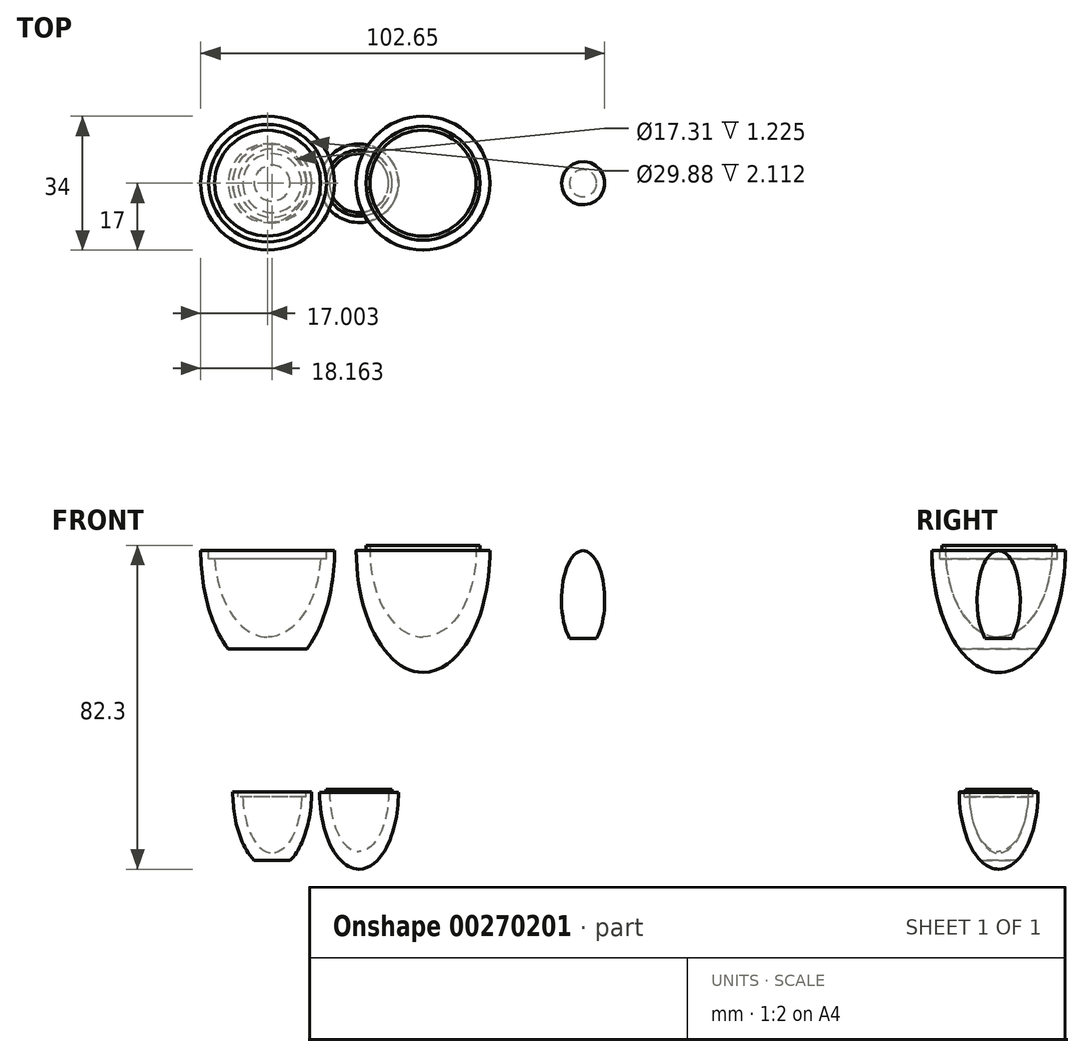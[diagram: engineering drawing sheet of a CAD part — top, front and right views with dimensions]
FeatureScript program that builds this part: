
annotation { "Feature Type Name" : "Feature", "Feature Type Description" : "" }
export const myFeature = defineFeature(function(context is Context, id is Id, definition is map)
    precondition{}
    {
        {
            var Q0;
            Q0=qCreatedBy(makeId("Front.planeOp"),FACE);
            var sketch = newSketch(context, id + "F0", { "sketchPlane" : qUnion([Q0])});
            skEllipse(sketch, "E0", {"center": v(-41.04, 45.75) * mm, "majorRadius": 31 * mm, "minorRadius": 17 * mm, "majorAxis": v(0, -1)});
            skEllipse(sketch, "E1", {"center": v(-41.04, 45.75) * mm, "majorRadius": 22 * mm, "minorRadius": 13.5 * mm, "majorAxis": v(0, -1)});
            skLineSegment(sketch, "E2", {"start": v(-65.22, 45.75) * mm, "end": v(-18.16, 45.75) * mm});
            skPoint(sketch, "E2.startSnap0", {"position": v(-58.04, 45.75) * mm});
            skPoint(sketch, "E2.endSnap0", {"position": v(-24.04, 45.75) * mm});
            skLineSegment(sketch, "E3", {"start": v(-56.07, 20.67) * mm, "end": v(-28.32, 20.67) * mm});
            skEllipse(sketch, "E4", {"center": v(-1.54, 45.76) * mm, "majorRadius": 31 * mm, "minorRadius": 17 * mm, "majorAxis": v(0, -1)});
            skEllipse(sketch, "E5", {"center": v(-1.54, 45.76) * mm, "majorRadius": 22 * mm, "minorRadius": 13.5 * mm, "majorAxis": v(0, -1)});
            skLineSegment(sketch, "E6", {"start": v(-25.72, 45.76) * mm, "end": v(21.34, 45.76) * mm});
            skPoint(sketch, "E6.startSnap0", {"position": v(-18.54, 45.76) * mm});
            skPoint(sketch, "E6.endSnap0", {"position": v(15.46, 45.76) * mm});
            skLineSegment(sketch, "E7", {"start": v(-15.6, 16.89) * mm, "end": v(12.15, 16.89) * mm});
            skLineSegment(sketch, "E8", {"start": v(-41.04, 45.75) * mm, "end": v(-41.04, 11.18) * mm});
            skPoint(sketch, "E8.endSnap0", {"position": v(-41.04, 14.75) * mm});
            skLineSegment(sketch, "E9", {"start": v(-41.04, 11.18) * mm, "end": v(-1.54, 11.18) * mm});
            skLineSegment(sketch, "E10", {"start": v(-1.54, 11.18) * mm, "end": v(-1.54, 45.76) * mm});
            skLineSegment(sketch, "E11", {"start": v(-55.97, 45.75) * mm, "end": v(-55.97, 43.64) * mm});
            skLineSegment(sketch, "E12", {"start": v(-55.97, 43.64) * mm, "end": v(-54.47, 43.64) * mm});
            skLineSegment(sketch, "E13", {"start": v(-16.01, 45.76) * mm, "end": v(-16.01, 47.05) * mm});
            skLineSegment(sketch, "E14", {"start": v(-16.01, 47.05) * mm, "end": v(-15.01, 47.05) * mm});
            skEllipse(sketch, "E15", {"center": v(-39.88, -15.66) * mm, "majorRadius": 19.5 * mm, "minorRadius": 10 * mm, "majorAxis": v(0, -1)});
            skEllipse(sketch, "E16", {"center": v(-39.88, -15.66) * mm, "majorRadius": 15.5 * mm, "minorRadius": 7.5 * mm, "majorAxis": v(0, -1)});
            skLineSegment(sketch, "E17", {"start": v(-39.88, 6.47) * mm, "end": v(-39.88, -39.32) * mm});
            skPoint(sketch, "E17.endSnap0", {"position": v(-39.88, -35.16) * mm});
            skLineSegment(sketch, "E18", {"start": v(-52.85, -15.66) * mm, "end": v(-28.62, -15.66) * mm});
            skPoint(sketch, "E18.startSnap0", {"position": v(-49.88, -15.66) * mm});
            skPoint(sketch, "E18.endSnap0", {"position": v(-29.88, -15.66) * mm});
            skLineSegment(sketch, "E19", {"start": v(-48.53, -13.93) * mm, "end": v(-48.53, -18) * mm});
            skLineSegment(sketch, "E20", {"start": v(-48.53, -13.93) * mm, "end": v(-47.33, -13.93) * mm});
            skEllipse(sketch, "E21", {"center": v(-17.8, -15.75) * mm, "majorRadius": 19.5 * mm, "minorRadius": 10 * mm, "majorAxis": v(0, -1)});
            skEllipse(sketch, "E22", {"center": v(-17.8, -15.75) * mm, "majorRadius": 15 * mm, "minorRadius": 7.5 * mm, "majorAxis": v(0, -1)});
            skLineSegment(sketch, "E23", {"start": v(-17.8, 6.39) * mm, "end": v(-17.8, -39.4) * mm});
            skPoint(sketch, "E23.endSnap0", {"position": v(-17.8, -35.25) * mm});
            skLineSegment(sketch, "E24", {"start": v(-30.78, -15.75) * mm, "end": v(-6.55, -15.75) * mm});
            skPoint(sketch, "E24.startSnap0", {"position": v(-27.8, -15.75) * mm});
            skPoint(sketch, "E24.endSnap0", {"position": v(-7.8, -15.75) * mm});
            skLineSegment(sketch, "E25", {"start": v(-27.21, -18.45) * mm, "end": v(-25.19, -18.45) * mm});
            skLineSegment(sketch, "E26", {"start": v(-49.95, -33) * mm, "end": v(-10.48, -33) * mm});
            skLineSegment(sketch, "E27", {"start": v(-26.2, -18.45) * mm, "end": v(-25.94, -18.45) * mm});
            skLineSegment(sketch, "E28", {"start": v(-26.2, -18.45) * mm, "end": v(-26.2, -14.54) * mm});
            skLineSegment(sketch, "E29", {"start": v(-48.53, -16.89) * mm, "end": v(-47.35, -16.89) * mm});
            skLineSegment(sketch, "E30", {"start": v(-26.2, -14.98) * mm, "end": v(-25.3, -14.98) * mm});
            skLineSegment(sketch, "E31.bottom", {"start": v(19.08, 0) * mm, "end": v(44.84, 0) * mm});
            skLineSegment(sketch, "E31.top", {"start": v(19.08, -50.96) * mm, "end": v(44.84, -50.96) * mm});
            skLineSegment(sketch, "E31.left", {"start": v(19.08, 0) * mm, "end": v(19.08, -50.96) * mm});
            skLineSegment(sketch, "E31.right", {"start": v(44.84, 0) * mm, "end": v(44.84, -50.96) * mm});
            skEllipse(sketch, "E32", {"center": v(29.53, -7.3) * mm, "majorRadius": 4.4 * mm, "minorRadius": 2.07 * mm, "majorAxis": v(0, -1)});
            skEllipse(sketch, "E33", {"center": v(39.11, 33.18) * mm, "majorRadius": 5.5 * mm, "minorRadius": 12.5 * mm, "majorAxis": v(1, 0)});
            skLineSegment(sketch, "E34", {"start": v(33.39, 20.02) * mm, "end": v(44.84, 20.02) * mm});
            skLineSegment(sketch, "E35", {"start": v(44.84, 20.02) * mm, "end": v(39.11, 14.3) * mm});
            skPoint(sketch, "E35.endSnap0", {"position": v(39.11, 45.68) * mm});
            skLineSegment(sketch, "E36", {"start": v(39.11, 14.3) * mm, "end": v(39.11, 50.35) * mm});
            skLineSegment(sketch, "E37", {"start": v(33.39, 23.45) * mm, "end": v(42.81, 23.45) * mm});
            skLineSegment(sketch, "E38", {"start": v(42.81, 23.45) * mm, "end": v(61.25, 10.67) * mm});
            skSolve(sketch);
        }
        {
            var Q0;
            {var subQ1=sQuery(id+"F0.wireOp",EDGE,"E0");var subQ5=sQuery(id+"F0.wireOp",EDGE,"E2");var subQ6=makeQuery(id+"F0.imprint","INTERSECT",VERTEX,{"disambiguationData":[OD(0.0)],"derivedFrom":[subQ1,subQ5]});Q0=makeQuery(id+"F0.imprint","IMPRINT",FACE,{"disambiguationData":[TD([[makeQuery(id+"F0.imprint","IMPRINT",EDGE,{"disambiguationData":[TD([[subQ6,-1.0]])],"derivedFrom":subQ1}),1.0]])]});}
            var Q1;
            Q1=sQuery(id+"F0.wireOp",EDGE,"E8");
            revolve(context, id + "F1", {"entities" : qUnion([Q0]), "axis" : qUnion([Q1]), "revolveType" : RevolveType.FULL});
        }
        {
            var Q0;
            {var subQ2=sQuery(id+"F0.wireOp",EDGE,"E4");var subQ4=makeQuery(id+"F0.imprint","INTERSECT",VERTEX,{"derivedFrom":[sQuery(id+"F0.wireOp",EDGE,"E2"),subQ2]});Q0=makeQuery(id+"F0.imprint","IMPRINT",FACE,{"disambiguationData":[TD([[makeQuery(id+"F0.imprint","IMPRINT",EDGE,{"disambiguationData":[TD([[subQ4,1.0]])],"derivedFrom":subQ2}),1.0]])]});}
            var Q1;
            {var subQ4=sQuery(id+"F0.wireOp",EDGE,"E13");Q1=makeQuery(id+"F0.imprint","IMPRINT",FACE,{"disambiguationData":[TD([[makeQuery(id+"F0.imprint","IMPRINT",EDGE,{"derivedFrom":subQ4}),-1.0]])]});}
            var Q2;
            {var subQ0=sQuery(id+"F0.wireOp",EDGE,"E10");var subQ1=sQuery(id+"F0.wireOp",EDGE,"E4");var subQ2=makeQuery(id+"F0.imprint","INTERSECT",VERTEX,{"derivedFrom":[subQ1,subQ0]});Q2=makeQuery(id+"F0.imprint","IMPRINT",FACE,{"disambiguationData":[TD([[makeQuery(id+"F0.imprint","IMPRINT",EDGE,{"disambiguationData":[TD([[subQ2,1.0]])],"derivedFrom":subQ1}),1.0]])]});}
            var Q3;
            Q3=sQuery(id+"F0.wireOp",EDGE,"E10");
            revolve(context, id + "F2", {"entities" : qUnion([Q0, Q1, Q2]), "axis" : qUnion([Q3]), "revolveType" : RevolveType.FULL});
        }
        {
            var Q0;
            {var subQ11=sQuery(id+"F0.wireOp",EDGE,"E29");Q0=makeQuery(id+"F0.imprint","IMPRINT",FACE,{"disambiguationData":[TD([[makeQuery(id+"F0.imprint","IMPRINT",EDGE,{"derivedFrom":subQ11}),-1.0]])]});}
            var Q1;
            Q1=sQuery(id+"F0.wireOp",EDGE,"E17");
            revolve(context, id + "F3", {"entities" : qUnion([Q0]), "axis" : qUnion([Q1]), "revolveType" : RevolveType.FULL});
        }
        {
            var Q0;
            {var subQ0=sQuery(id+"F0.wireOp",EDGE,"E30");Q0=makeQuery(id+"F0.imprint","IMPRINT",FACE,{"disambiguationData":[TD([[makeQuery(id+"F0.imprint","IMPRINT",EDGE,{"derivedFrom":subQ0}),-1.0]])]});}
            var Q1;
            {var subQ0=sQuery(id+"F0.wireOp",EDGE,"E25");var subQ1=sQuery(id+"F0.wireOp",EDGE,"E22");var subQ2=makeQuery(id+"F0.imprint","INTERSECT",VERTEX,{"derivedFrom":[subQ1,subQ0]});Q1=makeQuery(id+"F0.imprint","IMPRINT",FACE,{"disambiguationData":[TD([[makeQuery(id+"F0.imprint","IMPRINT",EDGE,{"disambiguationData":[TD([[subQ2,1.0]])],"derivedFrom":subQ1}),-1.0]])]});}
            var Q2;
            {var subQ7=sQuery(id+"F0.wireOp",EDGE,"E24");var subQ8=sQuery(id+"F0.wireOp",EDGE,"E21");var subQ9=makeQuery(id+"F0.imprint","INTERSECT",VERTEX,{"disambiguationData":[OD(1.0)],"derivedFrom":[subQ8,subQ7]});Q2=makeQuery(id+"F0.imprint","IMPRINT",FACE,{"disambiguationData":[TD([[makeQuery(id+"F0.imprint","IMPRINT",EDGE,{"disambiguationData":[TD([[subQ9,-1.0]])],"derivedFrom":subQ8}),1.0]])]});}
            var Q3;
            {var subQ0=sQuery(id+"F0.wireOp",EDGE,"E23");var subQ1=sQuery(id+"F0.wireOp",EDGE,"E21");var subQ2=makeQuery(id+"F0.imprint","INTERSECT",VERTEX,{"disambiguationData":[OD(0.0)],"derivedFrom":[subQ1,subQ0]});Q3=makeQuery(id+"F0.imprint","IMPRINT",FACE,{"disambiguationData":[TD([[makeQuery(id+"F0.imprint","IMPRINT",EDGE,{"disambiguationData":[TD([[subQ2,1.0]])],"derivedFrom":subQ1}),1.0]])]});}
            var Q4;
            Q4=sQuery(id+"F0.wireOp",EDGE,"E23");
            revolve(context, id + "F4", {"entities" : qUnion([Q0, Q1, Q2, Q3]), "axis" : qUnion([Q4]), "revolveType" : RevolveType.FULL});
        }
        {
            var Q0;
            {var subQ0=sQuery(id+"F0.wireOp",EDGE,"E37");var subQ1=sQuery(id+"F0.wireOp",EDGE,"E33");var subQ2=makeQuery(id+"F0.imprint","INTERSECT",VERTEX,{"disambiguationData":[OD(0.0)],"derivedFrom":[subQ1,subQ0]});Q0=makeQuery(id+"F0.imprint","IMPRINT",FACE,{"disambiguationData":[TD([[makeQuery(id+"F0.imprint","IMPRINT",EDGE,{"disambiguationData":[TD([[subQ2,1.0]])],"derivedFrom":subQ1}),1.0]])]});}
            var Q1;
            Q1=sQuery(id+"F0.wireOp",EDGE,"E36");
            revolve(context, id + "F5", {"entities" : qUnion([Q0]), "axis" : qUnion([Q1]), "revolveType" : RevolveType.FULL});
        }
    });
